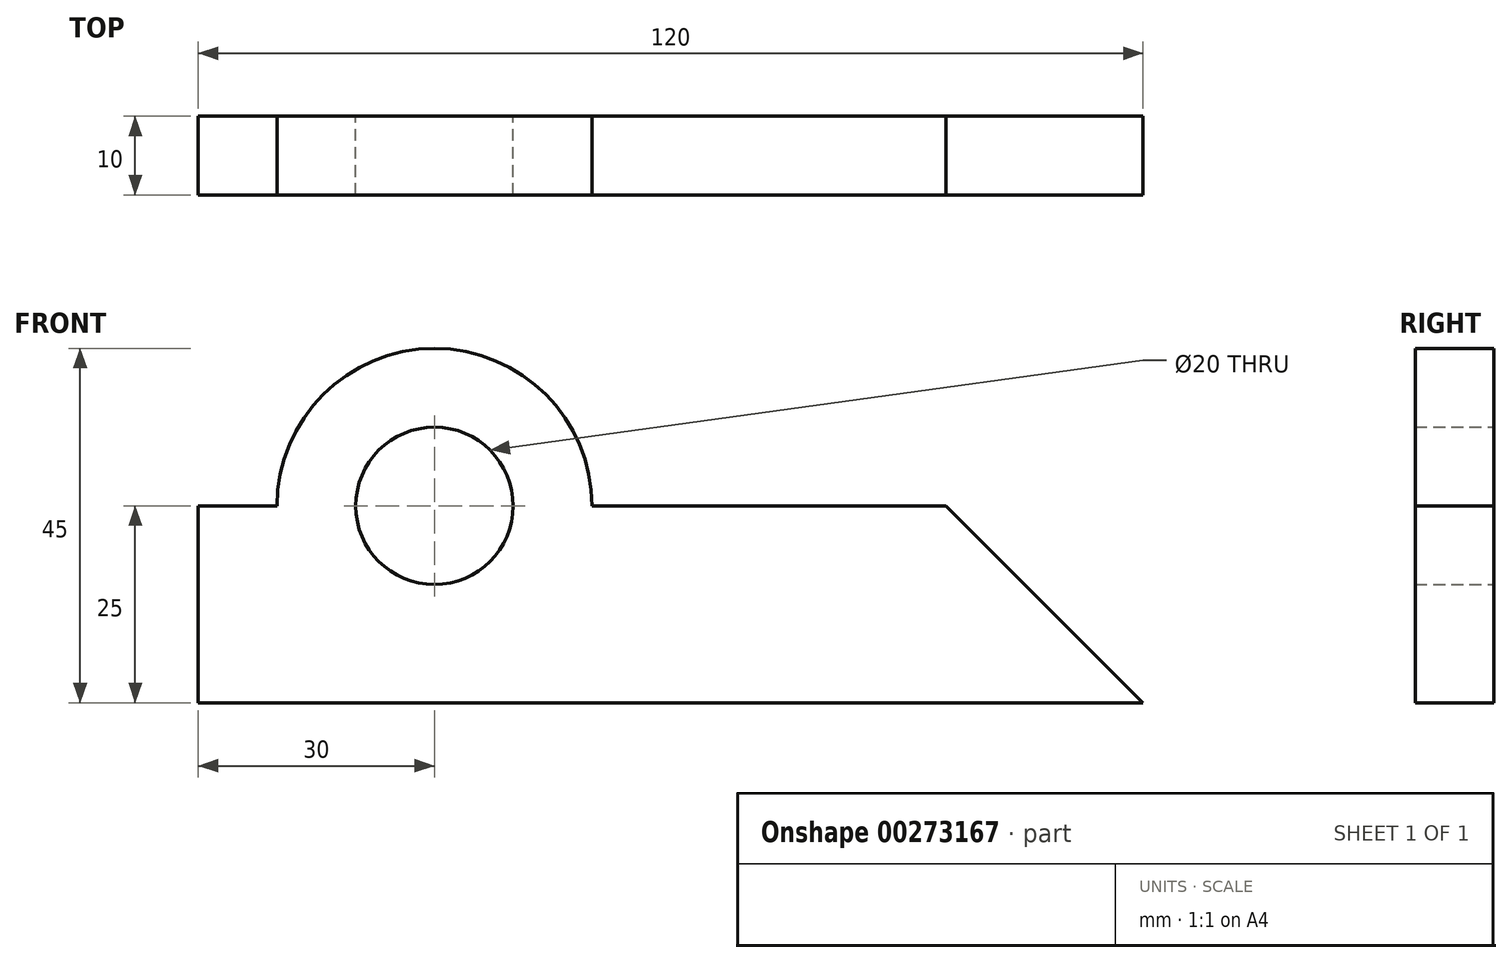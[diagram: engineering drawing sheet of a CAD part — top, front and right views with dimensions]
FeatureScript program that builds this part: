
annotation { "Feature Type Name" : "Feature", "Feature Type Description" : "" }
export const myFeature = defineFeature(function(context is Context, id is Id, definition is map)
    precondition{}
    {
        {
            var Q0;
            Q0=qCreatedBy(makeId("Front.planeOp"),FACE);
            var sketch = newSketch(context, id + "F0", { "sketchPlane" : qUnion([Q0])});
            skLineSegment(sketch, "E0", {"start": v(0, 0) * mm, "end": v(0, 25) * mm});
            skLineSegment(sketch, "E1", {"start": v(0, 25) * mm, "end": v(10, 25) * mm});
            skLineSegment(sketch, "E2", {"start": v(50, 25) * mm, "end": v(95, 25) * mm});
            skLineSegment(sketch, "E3", {"start": v(95, 25) * mm, "end": v(120, 0) * mm});
            skLineSegment(sketch, "E4", {"start": v(120, 0) * mm, "end": v(0, 0) * mm});
            skArc(sketch, "E5", {"start": v(50, 25) * mm, "mid": v(30, 45) * mm, "end": v(10, 25) * mm});
            skCircle(sketch, "E6", {"center": v(30, 25) * mm, "radius": 10 * mm});
            skSolve(sketch);
        }
        {
            var Q0;
            Q0 = qSketchRegion(id + "F0", true);
            extrude(context, id + "F1", {"entities" : qUnion([Q0]), "depth" : 10 * mm});
        }
    });
